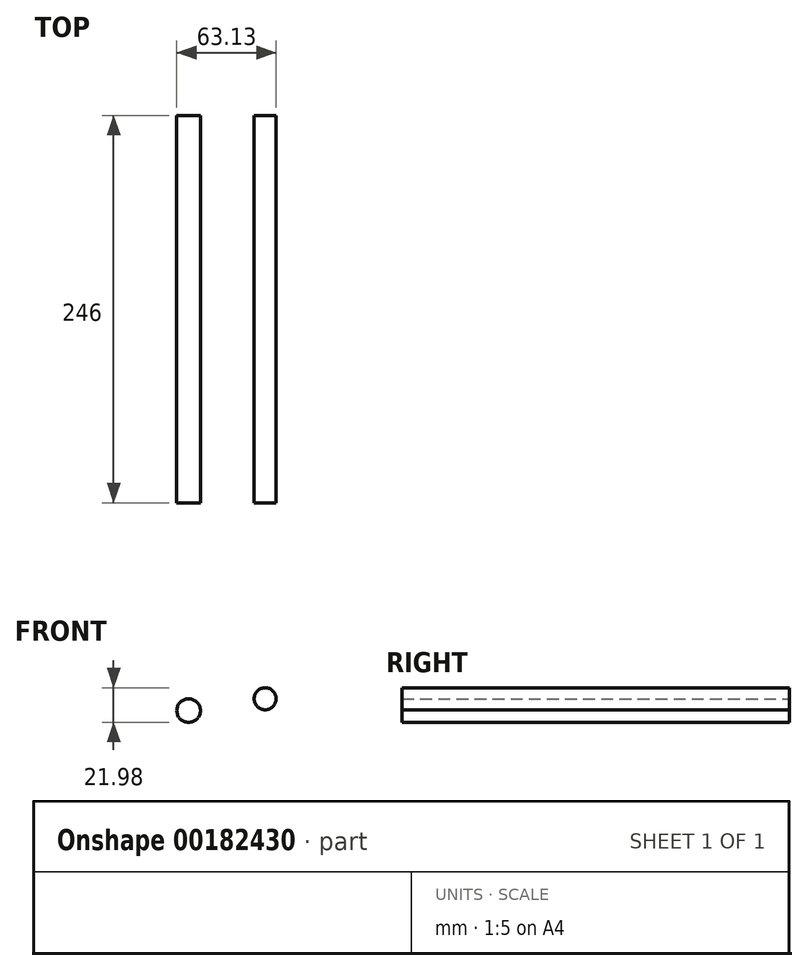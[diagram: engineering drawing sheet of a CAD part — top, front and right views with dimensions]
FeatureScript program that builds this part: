
annotation { "Feature Type Name" : "Feature", "Feature Type Description" : "" }
export const myFeature = defineFeature(function(context is Context, id is Id, definition is map)
    precondition{}
    {
        {
            var Q0;
            Q0=qCreatedBy(makeId("Front.planeOp"),FACE);
            var sketch = newSketch(context, id + "F0", { "sketchPlane" : qUnion([Q0])});
            skCircle(sketch, "E0", {"center": v(0, 0) * mm, "radius": 7.02 * mm});
            skSolve(sketch);
        }
        {
            var Q0;
            Q0 = qSketchRegion(id + "F0", true);
            extrude(context, id + "F1", {"entities" : qUnion([Q0]), "depth" : 100 * mm});
        }
        {
            var Q0;
            Q0=qCreatedBy(makeId("Front.planeOp"),FACE);
            var sketch = newSketch(context, id + "F2", { "sketchPlane" : qUnion([Q0])});
            skCircle(sketch, "E1", {"center": v(-48.6, -7.46) * mm, "radius": 7.5 * mm});
            skPoint(sketch, "E1.first.point", {"position": v(-47.85, 0) * mm});
            skPoint(sketch, "E1.second.point", {"position": v(-44.52, -13.75) * mm});
            skPoint(sketch, "E1.third.point", {"position": v(-49.36, 0) * mm});
            skSolve(sketch);
        }
        {
            var Q0;
            Q0 = qSketchRegion(id + "F2", true);
            extrude(context, id + "F3", {"entities" : qUnion([Q0]), "depth" : 25 * mm});
        }
        {
            var Q0;
            Q0=makeQuery(id+"F3.opExtrude","CAP_FACE",FACE,{"disambiguationData":[OSD([sQuery(id+"F2.wireOp",EDGE,"E1")])],"isStart":false});
            extrude(context, id + "F4", {"entities" : qUnion([Q0]), "operationType" : NewBodyOperationType.ADD, "depth" : 100 * mm});
        }
        {
            var Q0;
            Q0=makeQuery(id+"F1.opExtrude","CAP_FACE",FACE,{"disambiguationData":[OSD([sQuery(id+"F0.wireOp",EDGE,"E0")])],"isStart":false});
            extrude(context, id + "F5", {"entities" : qUnion([Q0]), "operationType" : NewBodyOperationType.ADD, "depth" : 100 * mm});
        }
        {
            var Q0;
            Q0=makeQuery(id+"F4.opExtrude","CAP_FACE",FACE,{"disambiguationData":[OSD([sQuery(id+"F2.wireOp",EDGE,"E1")])],"isStart":false});
            extrude(context, id + "F6", {"entities" : qUnion([Q0]), "operationType" : NewBodyOperationType.ADD, "depth" : 25 * mm});
        }
        {
            var Q0;
            Q0=makeQuery(id+"F6.opExtrude","CAP_FACE",FACE,{"disambiguationData":[OSD([sQuery(id+"F2.wireOp",EDGE,"E1")])],"isStart":false});
            extrude(context, id + "F7", {"entities" : qUnion([Q0]), "operationType" : NewBodyOperationType.ADD, "depth" : 70 * mm});
        }
        {
            var Q0;
            Q0=makeQuery(id+"F7.opExtrude","CAP_FACE",FACE,{"disambiguationData":[OSD([sQuery(id+"F2.wireOp",EDGE,"E1")])],"isStart":false});
            extrude(context, id + "F8", {"entities" : qUnion([Q0]), "operationType" : NewBodyOperationType.ADD, "depth" : 26 * mm});
        }
        {
            var Q0;
            Q0=makeQuery(id+"F5.opExtrude","CAP_FACE",FACE,{"disambiguationData":[OSD([sQuery(id+"F0.wireOp",EDGE,"E0")])],"isStart":false});
            extrude(context, id + "F9", {"entities" : qUnion([Q0]), "operationType" : NewBodyOperationType.ADD, "depth" : 46 * mm});
        }
    });
